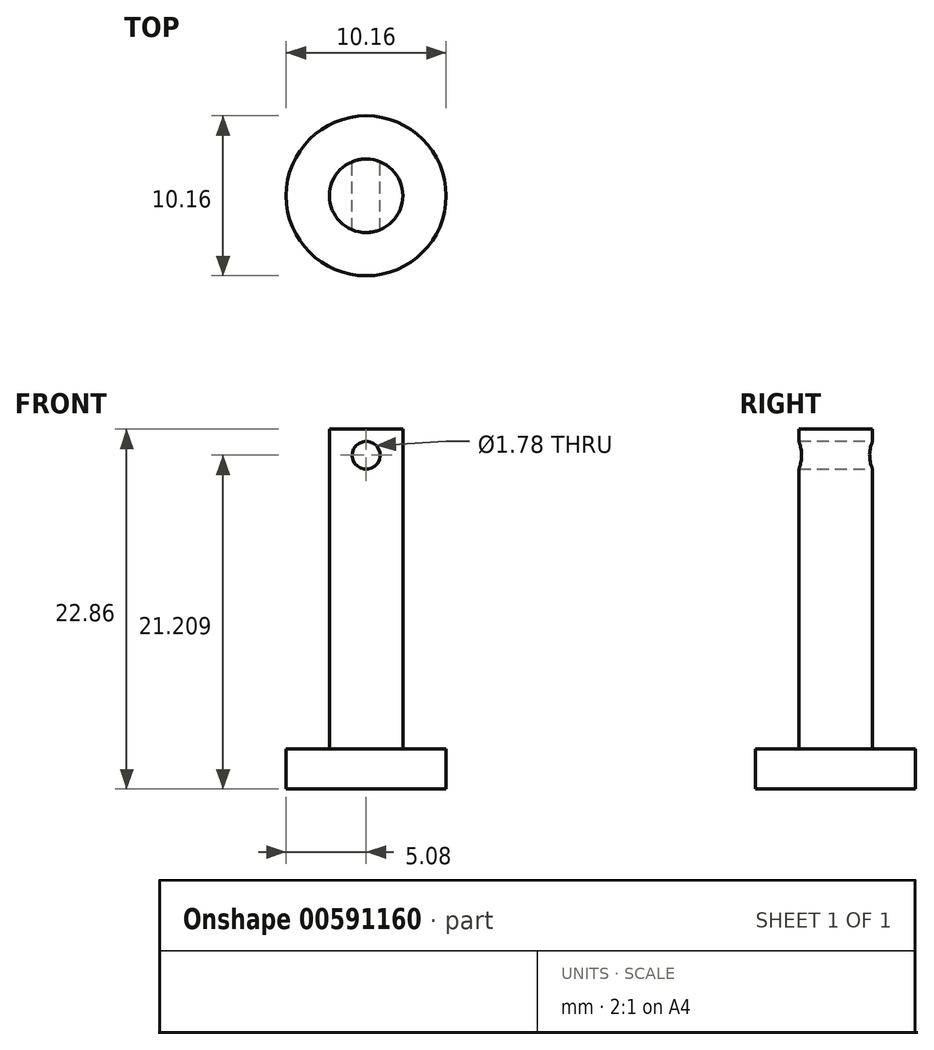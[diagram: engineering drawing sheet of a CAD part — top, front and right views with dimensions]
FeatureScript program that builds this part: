
annotation { "Feature Type Name" : "Feature", "Feature Type Description" : "" }
export const myFeature = defineFeature(function(context is Context, id is Id, definition is map)
    precondition{}
    {
        {
            var Q0;
            Q0=qCreatedBy(makeId("Top.planeOp"),FACE);
            var sketch = newSketch(context, id + "F0", { "sketchPlane" : qUnion([Q0])});
            skCircle(sketch, "E0", {"center": v(0, 0) * mm, "radius": 2.33 * mm});
            skSolve(sketch);
        }
        {
            var Q0;
            Q0=makeQuery(id+"F0.imprint","IMPRINT",FACE,{"disambiguationData":[TD([[makeQuery(id+"F0.imprint","IMPRINT",EDGE,{"derivedFrom":sQuery(id+"F0.wireOp",EDGE,"E0")}),1.0]])]});
            extrude(context, id + "F1", {"entities" : qUnion([Q0]), "depth" : 20.32 * mm, "offsetDistance" : 25.4 * mm});
        }
        {
            var Q0;
            Q0=makeQuery(id+"F1.opExtrude","CAP_FACE",FACE,{"disambiguationData":[OSD([sQuery(id+"F0.wireOp",EDGE,"E0")])],"isStart":true});
            var sketch = newSketch(context, id + "F2", { "sketchPlane" : qUnion([Q0])});
            skCircle(sketch, "E1", {"center": v(0, 0) * mm, "radius": 5.08 * mm});
            skSolve(sketch);
        }
        {
            var Q0;
            Q0=makeQuery(id+"F2.imprint","IMPRINT",FACE,{"disambiguationData":[TD([[makeQuery(id+"F2.imprint","IMPRINT",EDGE,{"derivedFrom":sQuery(id+"F2.wireOp",EDGE,"E1")}),1.0]])]});
            var Q1;
            Q1=makeQuery(id+"F2.imprint","IMPRINT",FACE,{"disambiguationData":[TD([[makeQuery(id+"F2.imprint","IMPRINT",EDGE,{"derivedFrom":makeQuery(id+"F1.opExtrude","CAP_EDGE",EDGE,{"disambiguationData":[OSD([sQuery(id+"F0.wireOp",EDGE,"E0")])],"isStart":true})}),-1.0]])]});
            extrude(context, id + "F3", {"entities" : qUnion([Q0, Q1]), "operationType" : NewBodyOperationType.ADD, "depth" : 2.54 * mm, "offsetDistance" : 25.4 * mm});
        }
        {
            var Q0;
            Q0=qCreatedBy(makeId("Front.planeOp"),FACE);
            var sketch = newSketch(context, id + "F4", { "sketchPlane" : qUnion([Q0])});
            skCircle(sketch, "E2", {"center": v(0, 18.67) * mm, "radius": 0.89 * mm});
            skSolve(sketch);
        }
        {
            var Q0;
            Q0 = qSketchRegion(id + "F4", true);
            extrude(context, id + "F5", {"entities" : qUnion([Q0]), "operationType" : NewBodyOperationType.REMOVE, "depth" : 25.4 * mm, "offsetDistance" : 25.4 * mm, "symmetric" : true});
        }
    });
